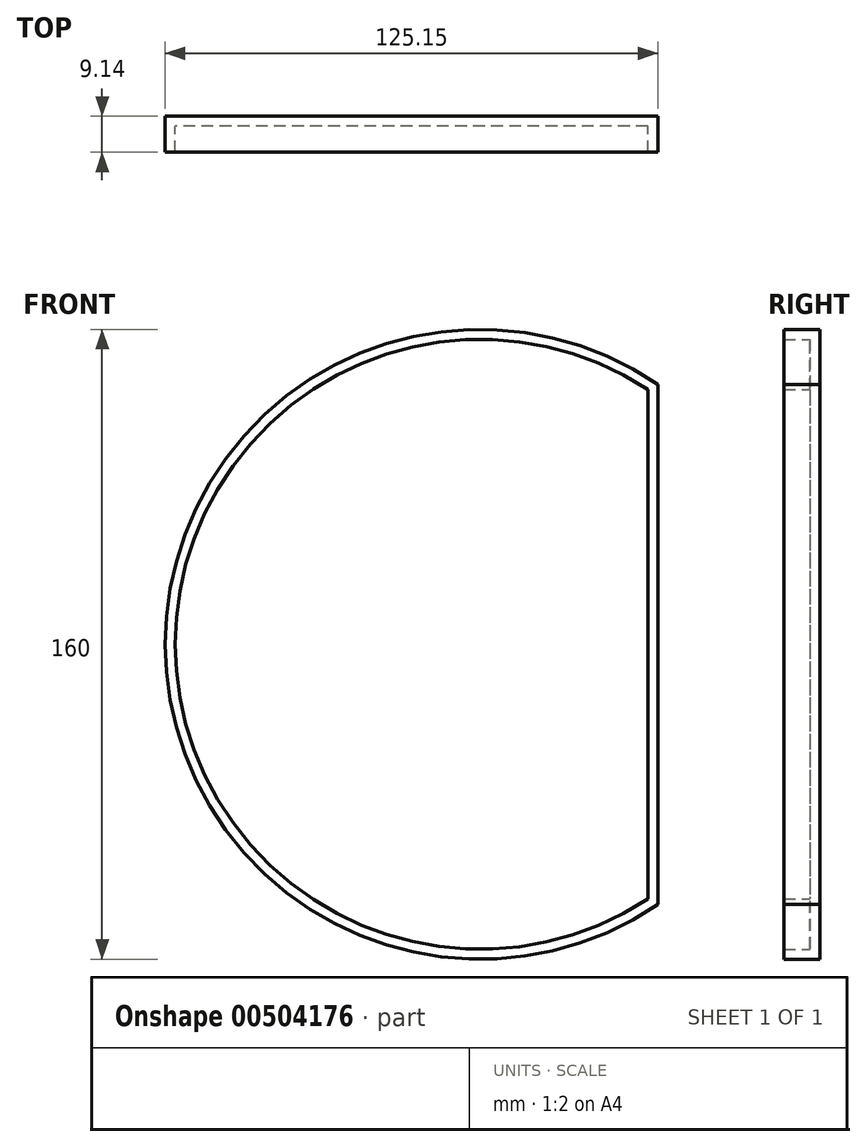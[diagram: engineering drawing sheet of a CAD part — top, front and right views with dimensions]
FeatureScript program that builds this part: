
annotation { "Feature Type Name" : "Feature", "Feature Type Description" : "" }
export const myFeature = defineFeature(function(context is Context, id is Id, definition is map)
    precondition{}
    {
        {
            var Q0;
            Q0=qCreatedBy(makeId("Front.planeOp"),FACE);
            var sketch = newSketch(context, id + "F0", { "sketchPlane" : qUnion([Q0])});
            skCircle(sketch, "E0", {"center": v(0, 0) * mm, "radius": 80 * mm});
            skLineSegment(sketch, "E1", {"start": v(45.15, 66.04) * mm, "end": v(45.15, -66.04) * mm});
            skSolve(sketch);
        }
        {
            var Q0;
            {var subQ0=sQuery(id+"F0.wireOp",EDGE,"E1");Q0=makeQuery(id+"F0.imprint","IMPRINT",FACE,{"disambiguationData":[TD([[makeQuery(id+"F0.imprint","IMPRINT",EDGE,{"derivedFrom":subQ0}),-1.0]])]});}
            extrude(context, id + "F1", {"entities" : qUnion([Q0]), "depth" : 9.14 * mm});
        }
        {
            var Q0;
            Q0=makeQuery(id+"F1.opExtrude","CAP_FACE",FACE,{"disambiguationData":[OSD([sQuery(id+"F0.wireOp",EDGE,"E0"),sQuery(id+"F0.wireOp",EDGE,"E1")])],"isStart":false});
            shell(context, id + "F2", {"entities" : qUnion([Q0]), "thickness" : 2.54 * mm});
        }
    });
